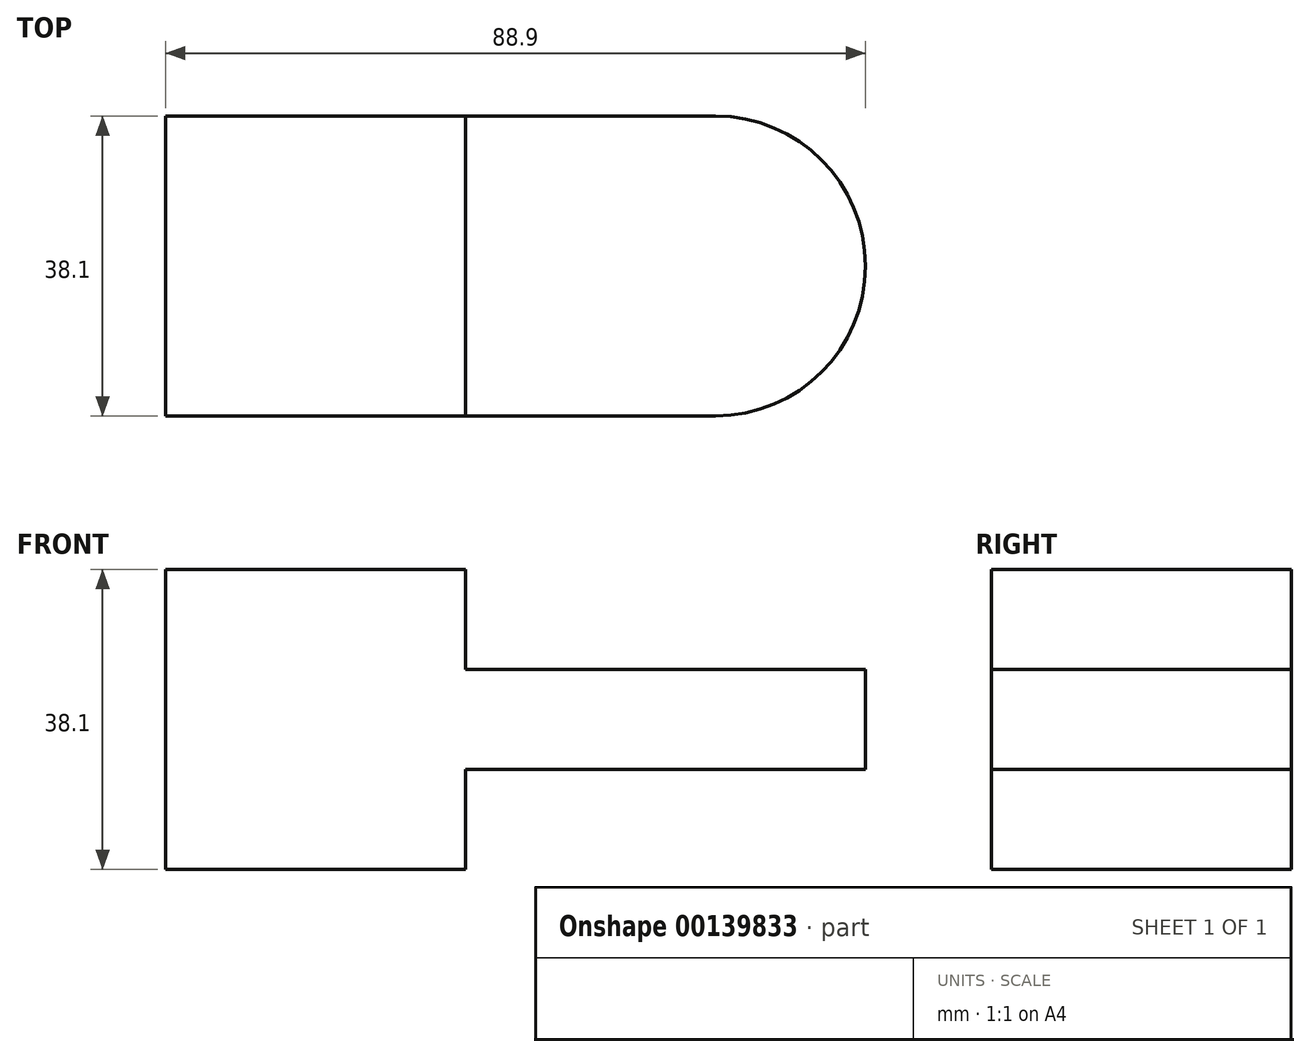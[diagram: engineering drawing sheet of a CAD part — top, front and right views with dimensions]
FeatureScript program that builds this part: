
annotation { "Feature Type Name" : "Feature", "Feature Type Description" : "" }
export const myFeature = defineFeature(function(context is Context, id is Id, definition is map)
    precondition{}
    {
        {
            var Q0;
            Q0=qCreatedBy(makeId("Front.planeOp"),FACE);
            var sketch = newSketch(context, id + "F0", { "sketchPlane" : qUnion([Q0])});
            skLineSegment(sketch, "E0", {"start": v(0, 0) * mm, "end": v(0, -38.1) * mm});
            skLineSegment(sketch, "E1", {"start": v(0, -38.1) * mm, "end": v(38.1, -38.1) * mm});
            skLineSegment(sketch, "E2", {"start": v(38.1, -38.1) * mm, "end": v(38.1, -25.4) * mm});
            skLineSegment(sketch, "E3", {"start": v(38.1, -25.4) * mm, "end": v(69.85, -25.4) * mm});
            skLineSegment(sketch, "E4", {"start": v(69.85, -25.4) * mm, "end": v(69.85, -12.7) * mm});
            skLineSegment(sketch, "E5", {"start": v(69.85, -12.7) * mm, "end": v(38.1, -12.7) * mm});
            skLineSegment(sketch, "E6", {"start": v(38.1, -12.7) * mm, "end": v(38.1, 0) * mm});
            skLineSegment(sketch, "E7", {"start": v(38.1, 0) * mm, "end": v(0, 0) * mm});
            skSolve(sketch);
        }
        {
            var Q0;
            Q0 = qSketchRegion(id + "F0", true);
            extrude(context, id + "F1", {"entities" : qUnion([Q0]), "oppositeDirection" : true, "depth" : 38.1 * mm});
        }
        {
            var Q0;
            Q0=makeQuery(id+"F1.opExtrude","SWEPT_FACE",FACE,{"disambiguationData":[OSD([sQuery(id+"F0.wireOp",EDGE,"E5")])]});
            var sketch = newSketch(context, id + "F2", { "sketchPlane" : qUnion([Q0])});
            skArc(sketch, "E8", {"start": v(69.85, 0) * mm, "mid": v(88.9, 19.05) * mm, "end": v(69.85, 38.1) * mm});
            skSolve(sketch);
        }
        {
            var Q0;
            Q0=makeQuery(id+"F2.imprint","IMPRINT",FACE,{"disambiguationData":[TD([[makeQuery(id+"F2.imprint","IMPRINT",EDGE,{"derivedFrom":sQuery(id+"F2.wireOp",EDGE,"E8")}),1.0]])]});
            var Q1;
            Q1=makeQuery(id+"F1.opExtrude","SWEPT_FACE",FACE,{"disambiguationData":[OSD([sQuery(id+"F0.wireOp",EDGE,"E3")])]});
            extrude(context, id + "F3", {"entities" : qUnion([Q0]), "operationType" : NewBodyOperationType.ADD, "endBound" : BoundingType.UP_TO_SURFACE, "oppositeDirection" : true, "endBoundEntityFace" : qUnion([Q1]), "depth" : 25.4 * mm});
        }
    });
